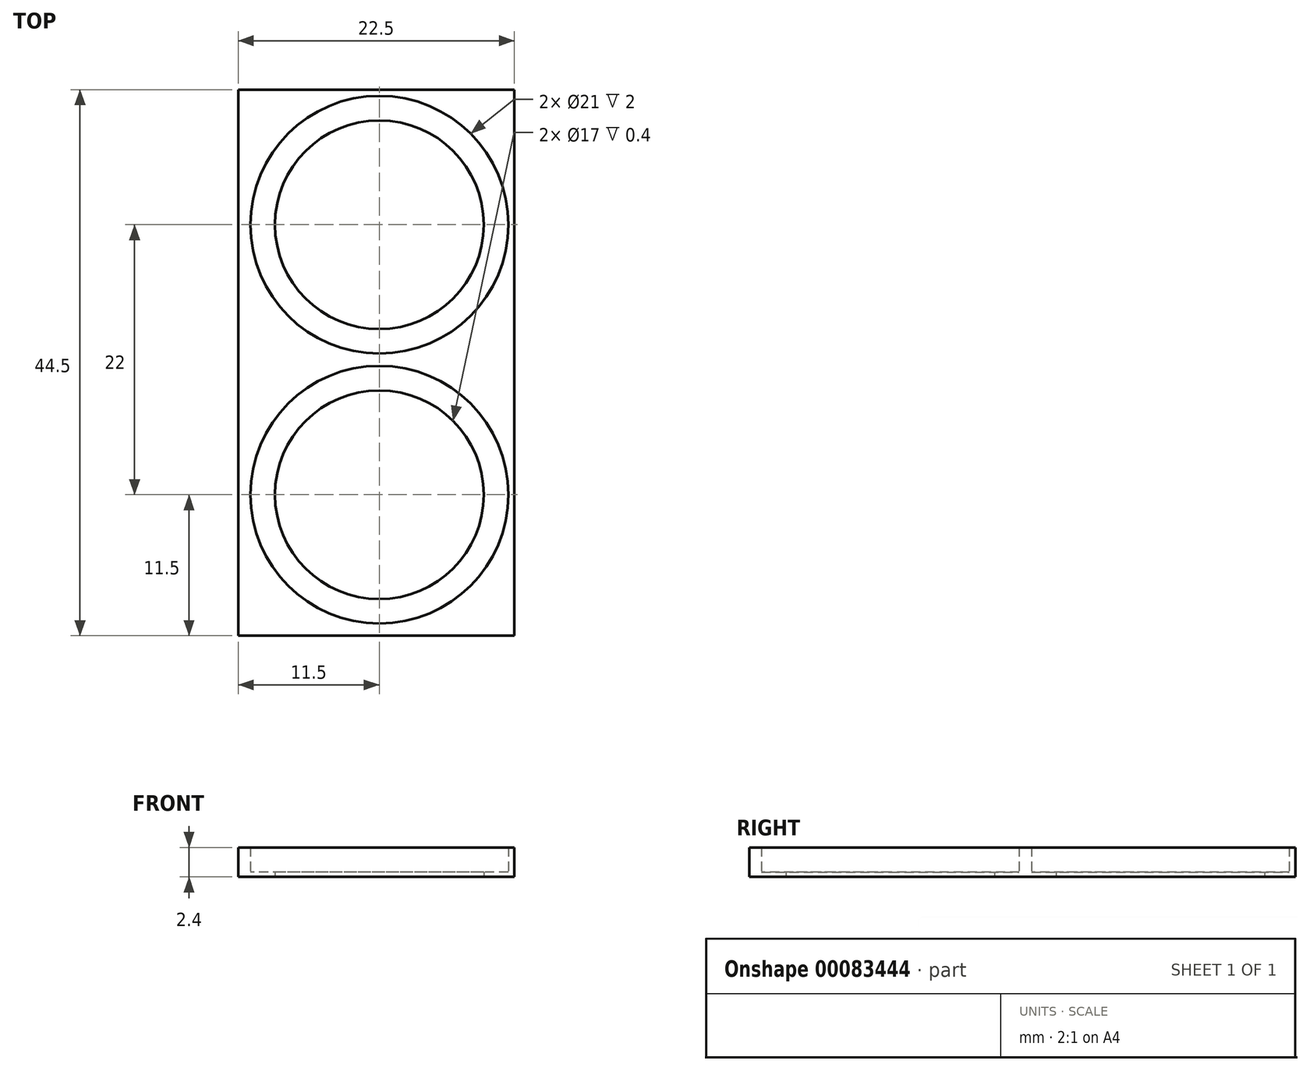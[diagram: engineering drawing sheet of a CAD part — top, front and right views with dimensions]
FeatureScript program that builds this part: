
annotation { "Feature Type Name" : "Feature", "Feature Type Description" : "" }
export const myFeature = defineFeature(function(context is Context, id is Id, definition is map)
    precondition{}
    {
        {
            assignVariable(context, id + "F0", {"name" : "size", "anyValue" : 21});
        }
        {
            var Q0;
            Q0=qCreatedBy(makeId("Top.planeOp"),FACE);
            var sketch = newSketch(context, id + "F1", { "sketchPlane" : qUnion([Q0])});
            skCircle(sketch, "E0", {"center": v(0, 0) * mm, "radius": 10.5 * mm});
            skCircle(sketch, "E1.0.1.0", {"center": v(0, 22) * mm, "radius": 10.5 * mm});
            skCircle(sketch, "E1.0.2.0", {"center": v(0, 44) * mm, "radius": 10.5 * mm});
            skCircle(sketch, "E1.0.3.0", {"center": v(0, 66) * mm, "radius": 10.5 * mm});
            skCircle(sketch, "E1.0.4.0", {"center": v(0, 88) * mm, "radius": 10.5 * mm});
            skCircle(sketch, "E1.1.0.0", {"center": v(22, 0) * mm, "radius": 10.5 * mm});
            skCircle(sketch, "E1.1.1.0", {"center": v(22, 22) * mm, "radius": 10.5 * mm});
            skCircle(sketch, "E1.1.2.0", {"center": v(22, 44) * mm, "radius": 10.5 * mm});
            skCircle(sketch, "E1.1.3.0", {"center": v(22, 66) * mm, "radius": 10.5 * mm});
            skCircle(sketch, "E1.1.4.0", {"center": v(22, 88) * mm, "radius": 10.5 * mm});
            skCircle(sketch, "E1.2.0.0", {"center": v(44, 0) * mm, "radius": 10.5 * mm});
            skCircle(sketch, "E1.2.1.0", {"center": v(44, 22) * mm, "radius": 10.5 * mm});
            skCircle(sketch, "E1.2.2.0", {"center": v(44, 44) * mm, "radius": 10.5 * mm});
            skCircle(sketch, "E1.2.3.0", {"center": v(44, 66) * mm, "radius": 10.5 * mm});
            skCircle(sketch, "E1.2.4.0", {"center": v(44, 88) * mm, "radius": 10.5 * mm});
            skCircle(sketch, "E1.3.0.0", {"center": v(66, 0) * mm, "radius": 10.5 * mm});
            skCircle(sketch, "E1.3.1.0", {"center": v(66, 22) * mm, "radius": 10.5 * mm});
            skCircle(sketch, "E1.3.2.0", {"center": v(66, 44) * mm, "radius": 10.5 * mm});
            skCircle(sketch, "E1.3.3.0", {"center": v(66, 66) * mm, "radius": 10.5 * mm});
            skCircle(sketch, "E1.3.4.0", {"center": v(66, 88) * mm, "radius": 10.5 * mm});
            skCircle(sketch, "E1.4.0.0", {"center": v(88, 0) * mm, "radius": 10.5 * mm});
            skCircle(sketch, "E1.4.1.0", {"center": v(88, 22) * mm, "radius": 10.5 * mm});
            skCircle(sketch, "E1.4.2.0", {"center": v(88, 44) * mm, "radius": 10.5 * mm});
            skCircle(sketch, "E1.4.3.0", {"center": v(88, 66) * mm, "radius": 10.5 * mm});
            skCircle(sketch, "E1.4.4.0", {"center": v(88, 88) * mm, "radius": 10.5 * mm});
            skCircle(sketch, "E1.5.0.0", {"center": v(110, 0) * mm, "radius": 10.5 * mm});
            skCircle(sketch, "E1.5.1.0", {"center": v(110, 22) * mm, "radius": 10.5 * mm});
            skCircle(sketch, "E1.5.2.0", {"center": v(110, 44) * mm, "radius": 10.5 * mm});
            skCircle(sketch, "E1.5.3.0", {"center": v(110, 66) * mm, "radius": 10.5 * mm});
            skCircle(sketch, "E1.5.4.0", {"center": v(110, 88) * mm, "radius": 10.5 * mm});
            skLineSegment(sketch, "E1.direction1", {"start": v(0, 0) * mm, "end": v(22, 0) * mm, "construction": true});
            skLineSegment(sketch, "E1.direction2", {"start": v(0, 0) * mm, "end": v(0, 22) * mm, "construction": true});
            skLineSegment(sketch, "E2.bottom", {"start": v(-11.5, 99.5) * mm, "end": v(121.5, 99.5) * mm});
            skLineSegment(sketch, "E2.top", {"start": v(-11.5, -11.5) * mm, "end": v(121.5, -11.5) * mm});
            skLineSegment(sketch, "E2.left", {"start": v(-11.5, 99.5) * mm, "end": v(-11.5, -11.5) * mm});
            skLineSegment(sketch, "E2.right", {"start": v(121.5, 99.5) * mm, "end": v(121.5, -11.5) * mm});
            skSolve(sketch);
        }
        {
            var Q0;
            Q0=makeQuery(id+"F1.imprint","IMPRINT",FACE,{"disambiguationData":[TD([[makeQuery(id+"F1.imprint","IMPRINT",EDGE,{"derivedFrom":sQuery(id+"F1.wireOp",EDGE,"E0")}),-1.0]])]});
            extrude(context, id + "F2", {"entities" : qUnion([Q0]), "depth" : 2 * mm});
        }
        {
            var Q0;
            Q0=makeQuery(id+"F2.opExtrude","CAP_FACE",FACE,{"disambiguationData":[OSD([sQuery(id+"F1.wireOp",EDGE,"E0"),sQuery(id+"F1.wireOp",EDGE,"E1.0.1.0"),sQuery(id+"F1.wireOp",EDGE,"E1.0.2.0"),sQuery(id+"F1.wireOp",EDGE,"E1.0.3.0"),sQuery(id+"F1.wireOp",EDGE,"E1.0.4.0"),sQuery(id+"F1.wireOp",EDGE,"E1.1.0.0"),sQuery(id+"F1.wireOp",EDGE,"E1.1.1.0"),sQuery(id+"F1.wireOp",EDGE,"E1.1.2.0"),sQuery(id+"F1.wireOp",EDGE,"E1.1.3.0"),sQuery(id+"F1.wireOp",EDGE,"E1.1.4.0"),sQuery(id+"F1.wireOp",EDGE,"E1.2.0.0"),sQuery(id+"F1.wireOp",EDGE,"E1.2.1.0"),sQuery(id+"F1.wireOp",EDGE,"E1.2.2.0"),sQuery(id+"F1.wireOp",EDGE,"E1.2.3.0"),sQuery(id+"F1.wireOp",EDGE,"E1.2.4.0"),sQuery(id+"F1.wireOp",EDGE,"E1.3.0.0"),sQuery(id+"F1.wireOp",EDGE,"E1.3.1.0"),sQuery(id+"F1.wireOp",EDGE,"E1.3.2.0"),sQuery(id+"F1.wireOp",EDGE,"E1.3.3.0"),sQuery(id+"F1.wireOp",EDGE,"E1.3.4.0"),sQuery(id+"F1.wireOp",EDGE,"E1.4.0.0"),sQuery(id+"F1.wireOp",EDGE,"E1.4.1.0"),sQuery(id+"F1.wireOp",EDGE,"E1.4.2.0"),sQuery(id+"F1.wireOp",EDGE,"E1.4.3.0"),sQuery(id+"F1.wireOp",EDGE,"E1.4.4.0"),sQuery(id+"F1.wireOp",EDGE,"E1.5.0.0"),sQuery(id+"F1.wireOp",EDGE,"E1.5.1.0"),sQuery(id+"F1.wireOp",EDGE,"E1.5.2.0"),sQuery(id+"F1.wireOp",EDGE,"E1.5.3.0"),sQuery(id+"F1.wireOp",EDGE,"E1.5.4.0"),sQuery(id+"F1.wireOp",EDGE,"E2.bottom"),sQuery(id+"F1.wireOp",EDGE,"E2.top"),sQuery(id+"F1.wireOp",EDGE,"E2.left"),sQuery(id+"F1.wireOp",EDGE,"E2.right")])],"isStart":false});
            var Q1;
            Q1=makeQuery(id+"F1.imprint","IMPRINT",FACE,{"disambiguationData":[TD([[makeQuery(id+"F1.imprint","IMPRINT",EDGE,{"derivedFrom":sQuery(id+"F1.wireOp",EDGE,"E1.0.4.0")}),1.0]])]});
            var Q2;
            Q2=makeQuery(id+"F1.imprint","IMPRINT",FACE,{"disambiguationData":[TD([[makeQuery(id+"F1.imprint","IMPRINT",EDGE,{"derivedFrom":sQuery(id+"F1.wireOp",EDGE,"E1.1.4.0")}),1.0]])]});
            var Q3;
            Q3=makeQuery(id+"F1.imprint","IMPRINT",FACE,{"disambiguationData":[TD([[makeQuery(id+"F1.imprint","IMPRINT",EDGE,{"derivedFrom":sQuery(id+"F1.wireOp",EDGE,"E1.2.4.0")}),1.0]])]});
            var Q4;
            Q4=makeQuery(id+"F1.imprint","IMPRINT",FACE,{"disambiguationData":[TD([[makeQuery(id+"F1.imprint","IMPRINT",EDGE,{"derivedFrom":sQuery(id+"F1.wireOp",EDGE,"E1.3.4.0")}),1.0]])]});
            var Q5;
            Q5=makeQuery(id+"F1.imprint","IMPRINT",FACE,{"disambiguationData":[TD([[makeQuery(id+"F1.imprint","IMPRINT",EDGE,{"derivedFrom":sQuery(id+"F1.wireOp",EDGE,"E1.4.4.0")}),1.0]])]});
            var Q6;
            Q6=makeQuery(id+"F1.imprint","IMPRINT",FACE,{"disambiguationData":[TD([[makeQuery(id+"F1.imprint","IMPRINT",EDGE,{"derivedFrom":sQuery(id+"F1.wireOp",EDGE,"E1.5.4.0")}),1.0]])]});
            var Q7;
            Q7=makeQuery(id+"F1.imprint","IMPRINT",FACE,{"disambiguationData":[TD([[makeQuery(id+"F1.imprint","IMPRINT",EDGE,{"derivedFrom":sQuery(id+"F1.wireOp",EDGE,"E1.5.3.0")}),1.0]])]});
            var Q8;
            Q8=makeQuery(id+"F1.imprint","IMPRINT",FACE,{"disambiguationData":[TD([[makeQuery(id+"F1.imprint","IMPRINT",EDGE,{"derivedFrom":sQuery(id+"F1.wireOp",EDGE,"E1.4.3.0")}),1.0]])]});
            var Q9;
            Q9=makeQuery(id+"F1.imprint","IMPRINT",FACE,{"disambiguationData":[TD([[makeQuery(id+"F1.imprint","IMPRINT",EDGE,{"derivedFrom":sQuery(id+"F1.wireOp",EDGE,"E1.3.3.0")}),1.0]])]});
            var Q10;
            Q10=makeQuery(id+"F1.imprint","IMPRINT",FACE,{"disambiguationData":[TD([[makeQuery(id+"F1.imprint","IMPRINT",EDGE,{"derivedFrom":sQuery(id+"F1.wireOp",EDGE,"E1.2.3.0")}),1.0]])]});
            var Q11;
            Q11=makeQuery(id+"F1.imprint","IMPRINT",FACE,{"disambiguationData":[TD([[makeQuery(id+"F1.imprint","IMPRINT",EDGE,{"derivedFrom":sQuery(id+"F1.wireOp",EDGE,"E1.1.3.0")}),1.0]])]});
            var Q12;
            Q12=makeQuery(id+"F1.imprint","IMPRINT",FACE,{"disambiguationData":[TD([[makeQuery(id+"F1.imprint","IMPRINT",EDGE,{"derivedFrom":sQuery(id+"F1.wireOp",EDGE,"E1.0.3.0")}),1.0]])]});
            var Q13;
            Q13=makeQuery(id+"F1.imprint","IMPRINT",FACE,{"disambiguationData":[TD([[makeQuery(id+"F1.imprint","IMPRINT",EDGE,{"derivedFrom":sQuery(id+"F1.wireOp",EDGE,"E1.1.2.0")}),1.0]])]});
            var Q14;
            Q14=makeQuery(id+"F1.imprint","IMPRINT",FACE,{"disambiguationData":[TD([[makeQuery(id+"F1.imprint","IMPRINT",EDGE,{"derivedFrom":sQuery(id+"F1.wireOp",EDGE,"E1.0.2.0")}),1.0]])]});
            var Q15;
            Q15=makeQuery(id+"F1.imprint","IMPRINT",FACE,{"disambiguationData":[TD([[makeQuery(id+"F1.imprint","IMPRINT",EDGE,{"derivedFrom":sQuery(id+"F1.wireOp",EDGE,"E1.2.2.0")}),1.0]])]});
            var Q16;
            Q16=makeQuery(id+"F1.imprint","IMPRINT",FACE,{"disambiguationData":[TD([[makeQuery(id+"F1.imprint","IMPRINT",EDGE,{"derivedFrom":sQuery(id+"F1.wireOp",EDGE,"E1.3.2.0")}),1.0]])]});
            var Q17;
            Q17=makeQuery(id+"F1.imprint","IMPRINT",FACE,{"disambiguationData":[TD([[makeQuery(id+"F1.imprint","IMPRINT",EDGE,{"derivedFrom":sQuery(id+"F1.wireOp",EDGE,"E1.4.2.0")}),1.0]])]});
            var Q18;
            Q18=makeQuery(id+"F1.imprint","IMPRINT",FACE,{"disambiguationData":[TD([[makeQuery(id+"F1.imprint","IMPRINT",EDGE,{"derivedFrom":sQuery(id+"F1.wireOp",EDGE,"E1.5.2.0")}),1.0]])]});
            var Q19;
            Q19=makeQuery(id+"F1.imprint","IMPRINT",FACE,{"disambiguationData":[TD([[makeQuery(id+"F1.imprint","IMPRINT",EDGE,{"derivedFrom":sQuery(id+"F1.wireOp",EDGE,"E1.5.1.0")}),1.0]])]});
            var Q20;
            Q20=makeQuery(id+"F1.imprint","IMPRINT",FACE,{"disambiguationData":[TD([[makeQuery(id+"F1.imprint","IMPRINT",EDGE,{"derivedFrom":sQuery(id+"F1.wireOp",EDGE,"E1.4.1.0")}),1.0]])]});
            var Q21;
            Q21=makeQuery(id+"F1.imprint","IMPRINT",FACE,{"disambiguationData":[TD([[makeQuery(id+"F1.imprint","IMPRINT",EDGE,{"derivedFrom":sQuery(id+"F1.wireOp",EDGE,"E1.3.1.0")}),1.0]])]});
            var Q22;
            Q22=makeQuery(id+"F1.imprint","IMPRINT",FACE,{"disambiguationData":[TD([[makeQuery(id+"F1.imprint","IMPRINT",EDGE,{"derivedFrom":sQuery(id+"F1.wireOp",EDGE,"E1.2.1.0")}),1.0]])]});
            var Q23;
            Q23=makeQuery(id+"F1.imprint","IMPRINT",FACE,{"disambiguationData":[TD([[makeQuery(id+"F1.imprint","IMPRINT",EDGE,{"derivedFrom":sQuery(id+"F1.wireOp",EDGE,"E1.1.1.0")}),1.0]])]});
            var Q24;
            Q24=makeQuery(id+"F1.imprint","IMPRINT",FACE,{"disambiguationData":[TD([[makeQuery(id+"F1.imprint","IMPRINT",EDGE,{"derivedFrom":sQuery(id+"F1.wireOp",EDGE,"E1.0.1.0")}),1.0]])]});
            var Q25;
            Q25=makeQuery(id+"F1.imprint","IMPRINT",FACE,{"disambiguationData":[TD([[makeQuery(id+"F1.imprint","IMPRINT",EDGE,{"derivedFrom":sQuery(id+"F1.wireOp",EDGE,"E0")}),1.0]])]});
            var Q26;
            Q26=makeQuery(id+"F1.imprint","IMPRINT",FACE,{"disambiguationData":[TD([[makeQuery(id+"F1.imprint","IMPRINT",EDGE,{"derivedFrom":sQuery(id+"F1.wireOp",EDGE,"E1.1.0.0")}),1.0]])]});
            var Q27;
            Q27=makeQuery(id+"F1.imprint","IMPRINT",FACE,{"disambiguationData":[TD([[makeQuery(id+"F1.imprint","IMPRINT",EDGE,{"derivedFrom":sQuery(id+"F1.wireOp",EDGE,"E1.2.0.0")}),1.0]])]});
            var Q28;
            Q28=makeQuery(id+"F1.imprint","IMPRINT",FACE,{"disambiguationData":[TD([[makeQuery(id+"F1.imprint","IMPRINT",EDGE,{"derivedFrom":sQuery(id+"F1.wireOp",EDGE,"E1.3.0.0")}),1.0]])]});
            var Q29;
            Q29=makeQuery(id+"F1.imprint","IMPRINT",FACE,{"disambiguationData":[TD([[makeQuery(id+"F1.imprint","IMPRINT",EDGE,{"derivedFrom":sQuery(id+"F1.wireOp",EDGE,"E1.4.0.0")}),1.0]])]});
            var Q30;
            Q30=makeQuery(id+"F1.imprint","IMPRINT",FACE,{"disambiguationData":[TD([[makeQuery(id+"F1.imprint","IMPRINT",EDGE,{"derivedFrom":sQuery(id+"F1.wireOp",EDGE,"E1.5.0.0")}),1.0]])]});
            extrude(context, id + "F3", {"entities" : qUnion([Q0, Q1, Q2, Q3, Q4, Q5, Q6, Q7, Q8, Q9, Q10, Q11, Q12, Q13, Q14, Q15, Q16, Q17, Q18, Q19, Q20, Q21, Q22, Q23, Q24, Q25, Q26, Q27, Q28, Q29, Q30]), "operationType" : NewBodyOperationType.ADD, "depth" : .4 * mm});
        }
        {
            var Q0;
            Q0=sQuery(id+"F1.wireOp",VERTEX,"E1.0.4.0.center");
            var Q1;
            Q1=sQuery(id+"F1.wireOp",VERTEX,"E1.1.4.0.center");
            var Q2;
            Q2=sQuery(id+"F1.wireOp",VERTEX,"E1.2.4.0.center");
            var Q3;
            Q3=sQuery(id+"F1.wireOp",VERTEX,"E1.3.4.0.center");
            var Q4;
            Q4=sQuery(id+"F1.wireOp",VERTEX,"E1.4.4.0.center");
            var Q5;
            Q5=sQuery(id+"F1.wireOp",VERTEX,"E1.5.4.0.center");
            var Q6;
            Q6=sQuery(id+"F1.wireOp",VERTEX,"E1.5.3.0.center");
            var Q7;
            Q7=sQuery(id+"F1.wireOp",VERTEX,"E1.4.3.0.center");
            var Q8;
            Q8=sQuery(id+"F1.wireOp",VERTEX,"E1.3.3.0.center");
            var Q9;
            Q9=sQuery(id+"F1.wireOp",VERTEX,"E1.2.3.0.center");
            var Q10;
            Q10=sQuery(id+"F1.wireOp",VERTEX,"E1.1.3.0.center");
            var Q11;
            Q11=sQuery(id+"F1.wireOp",VERTEX,"E1.0.3.0.center");
            var Q12;
            Q12=sQuery(id+"F1.wireOp",VERTEX,"E1.0.2.0.center");
            var Q13;
            Q13=sQuery(id+"F1.wireOp",VERTEX,"E1.1.2.0.center");
            var Q14;
            Q14=sQuery(id+"F1.wireOp",VERTEX,"E1.2.2.0.center");
            var Q15;
            Q15=sQuery(id+"F1.wireOp",VERTEX,"E1.3.2.0.center");
            var Q16;
            Q16=sQuery(id+"F1.wireOp",VERTEX,"E1.4.2.0.center");
            var Q17;
            Q17=sQuery(id+"F1.wireOp",VERTEX,"E1.5.2.0.center");
            var Q18;
            Q18=sQuery(id+"F1.wireOp",VERTEX,"E1.5.1.0.center");
            var Q19;
            Q19=sQuery(id+"F1.wireOp",VERTEX,"E1.4.1.0.center");
            var Q20;
            Q20=sQuery(id+"F1.wireOp",VERTEX,"E1.3.1.0.center");
            var Q21;
            Q21=sQuery(id+"F1.wireOp",VERTEX,"E1.2.1.0.center");
            var Q22;
            Q22=sQuery(id+"F1.wireOp",VERTEX,"E1.1.1.0.center");
            var Q23;
            Q23=sQuery(id+"F1.wireOp",VERTEX,"E1.direction2.end");
            var Q24;
            Q24=sQuery(id+"F1.wireOp",VERTEX,"E1.5.0.0.center");
            var Q25;
            Q25=sQuery(id+"F1.wireOp",VERTEX,"E1.4.0.0.center");
            var Q26;
            Q26=sQuery(id+"F1.wireOp",VERTEX,"E1.3.0.0.center");
            var Q27;
            Q27=sQuery(id+"F1.wireOp",VERTEX,"E1.2.0.0.center");
            var Q28;
            Q28=sQuery(id+"F1.wireOp",VERTEX,"E1.1.0.0.center");
            var Q29;
            Q29=sQuery(id+"F1.wireOp",VERTEX,"E1.direction1.start");
            var Q30;
            Q30=makeQuery(id+"F2.opExtrude","SWEPT_BODY",BODY,{"disambiguationData":[OSD([sQuery(id+"F1.wireOp",EDGE,"E0"),sQuery(id+"F1.wireOp",EDGE,"E1.0.1.0"),sQuery(id+"F1.wireOp",EDGE,"E1.0.2.0"),sQuery(id+"F1.wireOp",EDGE,"E1.0.3.0"),sQuery(id+"F1.wireOp",EDGE,"E1.0.4.0"),sQuery(id+"F1.wireOp",EDGE,"E1.1.0.0"),sQuery(id+"F1.wireOp",EDGE,"E1.1.1.0"),sQuery(id+"F1.wireOp",EDGE,"E1.1.2.0"),sQuery(id+"F1.wireOp",EDGE,"E1.1.3.0"),sQuery(id+"F1.wireOp",EDGE,"E1.1.4.0"),sQuery(id+"F1.wireOp",EDGE,"E1.2.0.0"),sQuery(id+"F1.wireOp",EDGE,"E1.2.1.0"),sQuery(id+"F1.wireOp",EDGE,"E1.2.2.0"),sQuery(id+"F1.wireOp",EDGE,"E1.2.3.0"),sQuery(id+"F1.wireOp",EDGE,"E1.2.4.0"),sQuery(id+"F1.wireOp",EDGE,"E1.3.0.0"),sQuery(id+"F1.wireOp",EDGE,"E1.3.1.0"),sQuery(id+"F1.wireOp",EDGE,"E1.3.2.0"),sQuery(id+"F1.wireOp",EDGE,"E1.3.3.0"),sQuery(id+"F1.wireOp",EDGE,"E1.3.4.0"),sQuery(id+"F1.wireOp",EDGE,"E1.4.0.0"),sQuery(id+"F1.wireOp",EDGE,"E1.4.1.0"),sQuery(id+"F1.wireOp",EDGE,"E1.4.2.0"),sQuery(id+"F1.wireOp",EDGE,"E1.4.3.0"),sQuery(id+"F1.wireOp",EDGE,"E1.4.4.0"),sQuery(id+"F1.wireOp",EDGE,"E1.5.0.0"),sQuery(id+"F1.wireOp",EDGE,"E1.5.1.0"),sQuery(id+"F1.wireOp",EDGE,"E1.5.2.0"),sQuery(id+"F1.wireOp",EDGE,"E1.5.3.0"),sQuery(id+"F1.wireOp",EDGE,"E1.5.4.0"),sQuery(id+"F1.wireOp",EDGE,"E2.bottom"),sQuery(id+"F1.wireOp",EDGE,"E2.top"),sQuery(id+"F1.wireOp",EDGE,"E2.left"),sQuery(id+"F1.wireOp",EDGE,"E2.right")])]});
            hole(context, id + "F4", {"style" : HoleStyle.SIMPLE, "endStyle" : HoleEndStyle.THROUGH, "oppositeDirection" : true, "holeDiameter" : (getVariable(context, 'size') - 4) * mm, "locations" : qUnion([Q0, Q1, Q2, Q3, Q4, Q5, Q6, Q7, Q8, Q9, Q10, Q11, Q12, Q13, Q14, Q15, Q16, Q17, Q18, Q19, Q20, Q21, Q22, Q23, Q24, Q25, Q26, Q27, Q28, Q29]), "scope" : qUnion([Q30]), "isTappedThrough" : true});
        }
        {
            var Q0;
            Q0=makeQuery(id+"F3.opExtrude","CAP_FACE",FACE,{"disambiguationData":[OSD([sQuery(id+"F1.wireOp",EDGE,"E0"),sQuery(id+"F1.wireOp",EDGE,"E1.0.1.0"),sQuery(id+"F1.wireOp",EDGE,"E1.0.2.0"),sQuery(id+"F1.wireOp",EDGE,"E1.0.3.0"),sQuery(id+"F1.wireOp",EDGE,"E1.0.4.0"),sQuery(id+"F1.wireOp",EDGE,"E1.1.0.0"),sQuery(id+"F1.wireOp",EDGE,"E1.1.1.0"),sQuery(id+"F1.wireOp",EDGE,"E1.1.2.0"),sQuery(id+"F1.wireOp",EDGE,"E1.1.3.0"),sQuery(id+"F1.wireOp",EDGE,"E1.1.4.0"),sQuery(id+"F1.wireOp",EDGE,"E1.2.0.0"),sQuery(id+"F1.wireOp",EDGE,"E1.2.1.0"),sQuery(id+"F1.wireOp",EDGE,"E1.2.2.0"),sQuery(id+"F1.wireOp",EDGE,"E1.2.3.0"),sQuery(id+"F1.wireOp",EDGE,"E1.2.4.0"),sQuery(id+"F1.wireOp",EDGE,"E1.3.0.0"),sQuery(id+"F1.wireOp",EDGE,"E1.3.1.0"),sQuery(id+"F1.wireOp",EDGE,"E1.3.2.0"),sQuery(id+"F1.wireOp",EDGE,"E1.3.3.0"),sQuery(id+"F1.wireOp",EDGE,"E1.3.4.0"),sQuery(id+"F1.wireOp",EDGE,"E1.4.0.0"),sQuery(id+"F1.wireOp",EDGE,"E1.4.1.0"),sQuery(id+"F1.wireOp",EDGE,"E1.4.2.0"),sQuery(id+"F1.wireOp",EDGE,"E1.4.3.0"),sQuery(id+"F1.wireOp",EDGE,"E1.4.4.0"),sQuery(id+"F1.wireOp",EDGE,"E1.5.0.0"),sQuery(id+"F1.wireOp",EDGE,"E1.5.1.0"),sQuery(id+"F1.wireOp",EDGE,"E1.5.2.0"),sQuery(id+"F1.wireOp",EDGE,"E1.5.3.0"),sQuery(id+"F1.wireOp",EDGE,"E1.5.4.0"),sQuery(id+"F1.wireOp",EDGE,"E2.bottom"),sQuery(id+"F1.wireOp",EDGE,"E2.top"),sQuery(id+"F1.wireOp",EDGE,"E2.left"),sQuery(id+"F1.wireOp",EDGE,"E2.right")])],"isStart":false});
            var sketch = newSketch(context, id + "F5", { "sketchPlane" : qUnion([Q0])});
            skLineSegment(sketch, "E3.bottom", {"start": v(-11.5, -11.5) * mm, "end": v(11, -11.5) * mm});
            skLineSegment(sketch, "E3.top", {"start": v(-11.5, 33) * mm, "end": v(11, 33) * mm});
            skLineSegment(sketch, "E3.left", {"start": v(-11.5, -11.5) * mm, "end": v(-11.5, 33) * mm});
            skLineSegment(sketch, "E3.right", {"start": v(11, -11.5) * mm, "end": v(11, 33) * mm});
            skSolve(sketch);
        }
        {
            var Q0;
            Q0 = qSketchRegion(id + "F5", true);
            extrude(context, id + "F6", {"entities" : qUnion([Q0]), "operationType" : NewBodyOperationType.INTERSECT, "oppositeDirection" : true, "depth" : 25 * mm});
        }
    });
